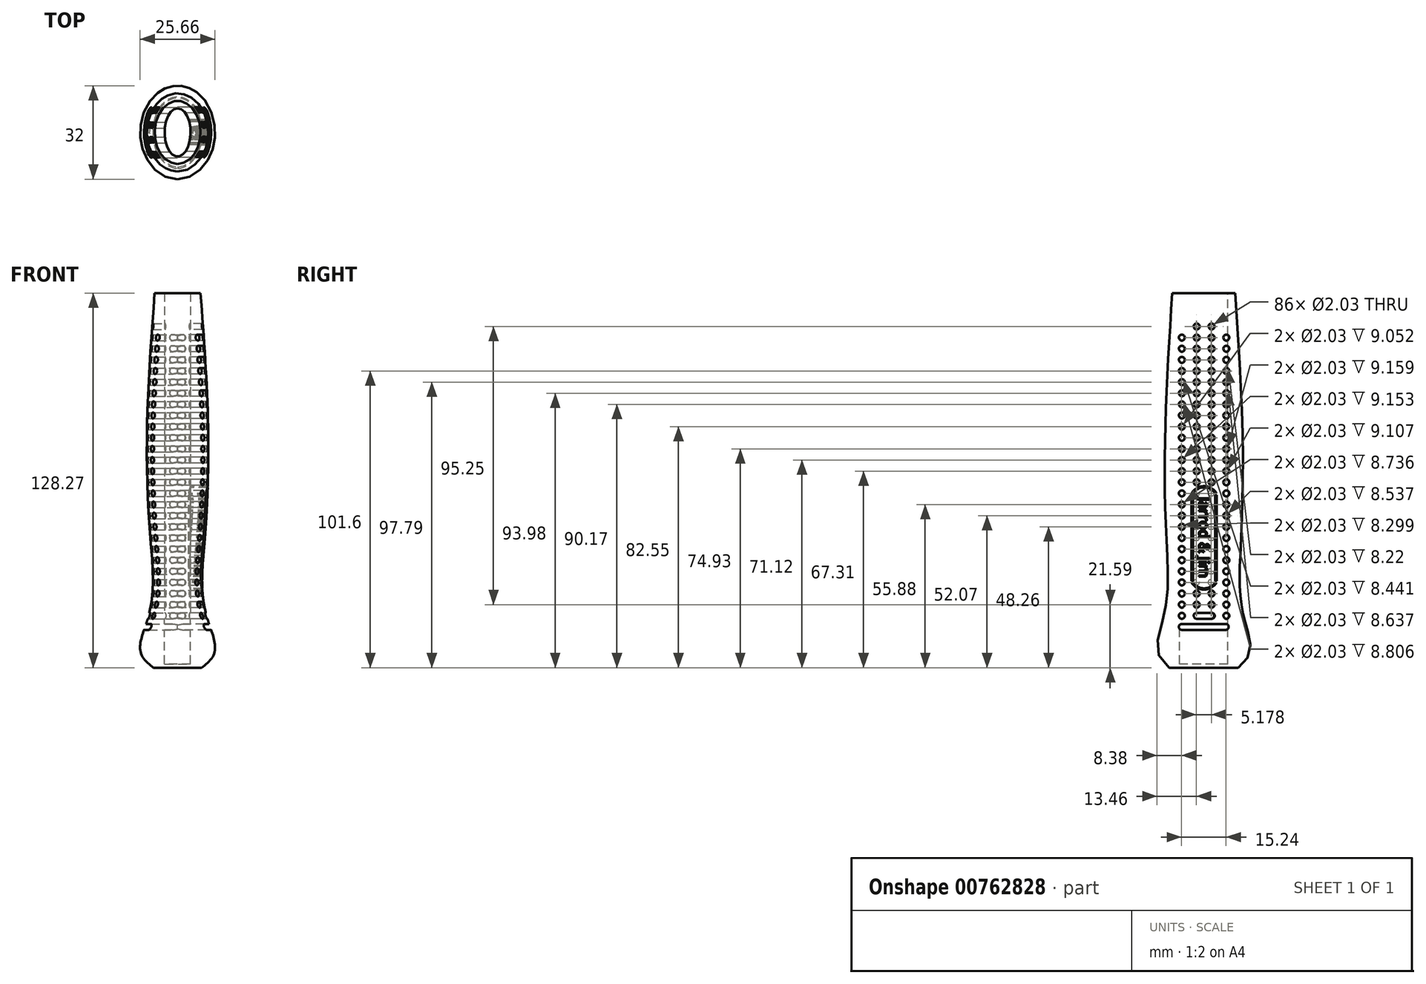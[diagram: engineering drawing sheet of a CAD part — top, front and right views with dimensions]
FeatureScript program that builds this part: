
annotation { "Feature Type Name" : "Feature", "Feature Type Description" : "" }
export const myFeature = defineFeature(function(context is Context, id is Id, definition is map)
    precondition{}
    {
        {
            var Q0;
            Q0=qCreatedBy(makeId("Top.planeOp"),FACE);
            var sketch = newSketch(context, id + "F0", { "sketchPlane" : qUnion([Q0])});
            skEllipse(sketch, "E0", {"center": v(0, 0) * mm, "majorRadius": 11.81 * mm, "minorRadius": 8.26 * mm, "majorAxis": v(0, -1)});
            skSolve(sketch);
        }
        {
            var Q0;
            Q0=qCreatedBy(makeId("Top.planeOp"),FACE);
            cPlane(context, id + "F1", {"entities" : qUnion([Q0]), "cplaneType" : CPlaneType.OFFSET, "offset" : 3.8 * mm, "width" : 152.4 * mm, "height" : 152.4 * mm});
        }
        {
            var Q0;
            Q0=qCreatedBy(id+"F1.planeOp",FACE);
            var sketch = newSketch(context, id + "F2", { "sketchPlane" : qUnion([Q0])});
            skEllipse(sketch, "E1", {"center": v(0, 0) * mm, "majorRadius": 15.24 * mm, "minorRadius": 12.07 * mm, "majorAxis": v(0, -1)});
            skSolve(sketch);
        }
        {
            var Q0;
            Q0=qCreatedBy(id+"F1.planeOp",FACE);
            cPlane(context, id + "F3", {"entities" : qUnion([Q0]), "cplaneType" : CPlaneType.OFFSET, "offset" : 12.7 * mm, "width" : 152.4 * mm, "height" : 152.4 * mm});
        }
        {
            var Q0;
            Q0=qCreatedBy(id+"F3.planeOp",FACE);
            var sketch = newSketch(context, id + "F4", { "sketchPlane" : qUnion([Q0])});
            skEllipse(sketch, "E2", {"center": v(0, 0) * mm, "majorRadius": 13.97 * mm, "minorRadius": 10.29 * mm, "majorAxis": v(0, -1)});
            skSolve(sketch);
        }
        {
            var Q0;
            Q0=qCreatedBy(id+"F3.planeOp",FACE);
            cPlane(context, id + "F5", {"entities" : qUnion([Q0]), "cplaneType" : CPlaneType.OFFSET, "offset" : 25.4 * mm, "width" : 152.4 * mm, "height" : 152.4 * mm});
        }
        {
            var Q0;
            Q0=qCreatedBy(id+"F5.planeOp",FACE);
            var sketch = newSketch(context, id + "F6", { "sketchPlane" : qUnion([Q0])});
            skEllipse(sketch, "E3", {"center": v(0, 0) * mm, "majorRadius": 12.7 * mm, "minorRadius": 9.14 * mm, "majorAxis": v(0, -1)});
            skSolve(sketch);
        }
        {
            var Q0;
            Q0=qCreatedBy(id+"F5.planeOp",FACE);
            cPlane(context, id + "F7", {"entities" : qUnion([Q0]), "cplaneType" : CPlaneType.OFFSET, "offset" : 33.02 * mm, "width" : 152.4 * mm, "height" : 152.4 * mm});
        }
        {
            var Q0;
            Q0=qCreatedBy(id+"F7.planeOp",FACE);
            var sketch = newSketch(context, id + "F8", { "sketchPlane" : qUnion([Q0])});
            skEllipse(sketch, "E4", {"center": v(0, 0) * mm, "majorRadius": 13.34 * mm, "minorRadius": 10.54 * mm, "majorAxis": v(0, -1)});
            skSolve(sketch);
        }
        {
            var Q0;
            Q0=qCreatedBy(id+"F7.planeOp",FACE);
            cPlane(context, id + "F9", {"entities" : qUnion([Q0]), "cplaneType" : CPlaneType.OFFSET, "offset" : 53.34 * mm, "width" : 152.4 * mm, "height" : 152.4 * mm});
        }
        {
            var Q0;
            Q0=qCreatedBy(id+"F9.planeOp",FACE);
            var sketch = newSketch(context, id + "F10", { "sketchPlane" : qUnion([Q0])});
            skEllipse(sketch, "E5", {"center": v(0, 0) * mm, "majorRadius": 10.8 * mm, "minorRadius": 7.87 * mm, "majorAxis": v(0, -1)});
            skSolve(sketch);
        }
        {
            var Q0;
            Q0=makeQuery(id+"F0.imprint","IMPRINT",FACE,{"disambiguationData":[TD([[makeQuery(id+"F0.imprint","IMPRINT",EDGE,{"derivedFrom":sQuery(id+"F0.wireOp",EDGE,"E0")}),1.0]])]});
            var Q1;
            Q1=makeQuery(id+"F2.imprint","IMPRINT",FACE,{"disambiguationData":[TD([[makeQuery(id+"F2.imprint","IMPRINT",EDGE,{"derivedFrom":sQuery(id+"F2.wireOp",EDGE,"E1")}),1.0]])]});
            var Q2;
            Q2=makeQuery(id+"F4.imprint","IMPRINT",FACE,{"disambiguationData":[TD([[makeQuery(id+"F4.imprint","IMPRINT",EDGE,{"derivedFrom":sQuery(id+"F4.wireOp",EDGE,"E2")}),1.0]])]});
            var Q3;
            Q3=makeQuery(id+"F6.imprint","IMPRINT",FACE,{"disambiguationData":[TD([[makeQuery(id+"F6.imprint","IMPRINT",EDGE,{"derivedFrom":sQuery(id+"F6.wireOp",EDGE,"E3")}),1.0]])]});
            var Q4;
            Q4=makeQuery(id+"F8.imprint","IMPRINT",FACE,{"disambiguationData":[TD([[makeQuery(id+"F8.imprint","IMPRINT",EDGE,{"derivedFrom":sQuery(id+"F8.wireOp",EDGE,"E4")}),1.0]])]});
            var Q5;
            Q5=makeQuery(id+"F10.imprint","IMPRINT",FACE,{"disambiguationData":[TD([[makeQuery(id+"F10.imprint","IMPRINT",EDGE,{"derivedFrom":sQuery(id+"F10.wireOp",EDGE,"E5")}),1.0]])]});
            loft(context, id + "F11", {"sheetProfilesArray" : [{ "sheetProfileEntities" : qUnion([Q0]) }, { "sheetProfileEntities" : qUnion([Q1]) }, { "sheetProfileEntities" : qUnion([Q2]) }, { "sheetProfileEntities" : qUnion([Q3]) }, { "sheetProfileEntities" : qUnion([Q4]) }, { "sheetProfileEntities" : qUnion([Q5]) }]});
        }
        {
            var Q0;
            Q0=makeQuery(id+"F11.opLoft","CAP_FACE",FACE,{"disambiguationData":[OSD([makeQuery(id+"F10.imprint","IMPRINT",FACE,{"disambiguationData":[TD([[makeQuery(id+"F10.imprint","IMPRINT",EDGE,{"derivedFrom":sQuery(id+"F10.wireOp",EDGE,"E5")}),1.0]])]})])],"isStart":true});
            var sketch = newSketch(context, id + "F12", { "sketchPlane" : qUnion([Q0])});
            skEllipse(sketch, "E6", {"center": v(0, 0) * mm, "majorRadius": 4.45 * mm, "minorRadius": 8.26 * mm, "majorAxis": v(1, 0)});
            skSolve(sketch);
        }
        {
            var Q0;
            Q0=makeQuery(id+"F12.imprint","IMPRINT",FACE,{"disambiguationData":[TD([[makeQuery(id+"F12.imprint","IMPRINT",EDGE,{"derivedFrom":sQuery(id+"F12.wireOp",EDGE,"E6")}),1.0]])]});
            extrude(context, id + "F13", {"entities" : qUnion([Q0]), "operationType" : NewBodyOperationType.REMOVE, "oppositeDirection" : true, "depth" : 127 * mm, "offsetDistance" : 25.4 * mm});
        }
        {
            var Q0;
            Q0=qCreatedBy(makeId("Right.planeOp"),FACE);
            var sketch = newSketch(context, id + "F14", { "sketchPlane" : qUnion([Q0])});
            skCircle(sketch, "E7", {"center": v(-7.62, 17.78) * mm, "radius": 1.02 * mm});
            skCircle(sketch, "E8.0.1.0", {"center": v(-7.62, 21.59) * mm, "radius": 1.02 * mm});
            skCircle(sketch, "E8.0.2.0", {"center": v(-7.62, 25.4) * mm, "radius": 1.02 * mm});
            skCircle(sketch, "E8.0.3.0", {"center": v(-7.62, 29.21) * mm, "radius": 1.02 * mm});
            skCircle(sketch, "E8.0.4.0", {"center": v(-7.62, 33.02) * mm, "radius": 1.02 * mm});
            skCircle(sketch, "E8.0.5.0", {"center": v(-7.62, 36.83) * mm, "radius": 1.02 * mm});
            skCircle(sketch, "E8.0.6.0", {"center": v(-7.62, 40.64) * mm, "radius": 1.02 * mm});
            skCircle(sketch, "E8.0.7.0", {"center": v(-7.62, 44.45) * mm, "radius": 1.02 * mm});
            skCircle(sketch, "E8.0.8.0", {"center": v(-7.62, 48.26) * mm, "radius": 1.02 * mm});
            skCircle(sketch, "E8.0.9.0", {"center": v(-7.62, 52.07) * mm, "radius": 1.02 * mm});
            skCircle(sketch, "E8.0.10.0", {"center": v(-7.62, 55.88) * mm, "radius": 1.02 * mm});
            skCircle(sketch, "E8.0.11.0", {"center": v(-7.62, 59.7) * mm, "radius": 1.02 * mm});
            skCircle(sketch, "E8.0.12.0", {"center": v(-7.62, 63.5) * mm, "radius": 1.02 * mm});
            skCircle(sketch, "E8.0.13.0", {"center": v(-7.62, 67.31) * mm, "radius": 1.02 * mm});
            skCircle(sketch, "E8.0.14.0", {"center": v(-7.62, 71.12) * mm, "radius": 1.02 * mm});
            skCircle(sketch, "E8.0.15.0", {"center": v(-7.62, 74.93) * mm, "radius": 1.02 * mm});
            skCircle(sketch, "E8.0.16.0", {"center": v(-7.62, 78.74) * mm, "radius": 1.02 * mm});
            skCircle(sketch, "E8.0.17.0", {"center": v(-7.62, 82.55) * mm, "radius": 1.02 * mm});
            skCircle(sketch, "E8.0.18.0", {"center": v(-7.62, 86.36) * mm, "radius": 1.02 * mm});
            skCircle(sketch, "E8.0.19.0", {"center": v(-7.62, 90.17) * mm, "radius": 1.02 * mm});
            skCircle(sketch, "E8.0.20.0", {"center": v(-7.62, 93.98) * mm, "radius": 1.02 * mm});
            skCircle(sketch, "E8.0.21.0", {"center": v(-7.62, 97.8) * mm, "radius": 1.02 * mm});
            skCircle(sketch, "E8.0.22.0", {"center": v(-7.62, 101.6) * mm, "radius": 1.02 * mm});
            skCircle(sketch, "E8.0.23.0", {"center": v(-7.62, 105.41) * mm, "radius": 1.02 * mm});
            skCircle(sketch, "E8.0.24.0", {"center": v(-7.62, 109.22) * mm, "radius": 1.02 * mm});
            skCircle(sketch, "E8.0.25.0", {"center": v(-7.62, 113.03) * mm, "radius": 1.02 * mm});
            skCircle(sketch, "E8.1.1.0", {"center": v(-2.54, 21.59) * mm, "radius": 1.02 * mm});
            skCircle(sketch, "E8.1.2.0", {"center": v(-2.54, 25.4) * mm, "radius": 1.02 * mm});
            skCircle(sketch, "E8.1.3.0", {"center": v(-2.54, 29.21) * mm, "radius": 1.02 * mm});
            skCircle(sketch, "E8.1.4.0", {"center": v(-2.54, 33.02) * mm, "radius": 1.02 * mm});
            skCircle(sketch, "E8.1.5.0", {"center": v(-2.54, 36.83) * mm, "radius": 1.02 * mm});
            skCircle(sketch, "E8.1.6.0", {"center": v(-2.54, 40.64) * mm, "radius": 1.02 * mm});
            skCircle(sketch, "E8.1.7.0", {"center": v(-2.54, 44.45) * mm, "radius": 1.02 * mm});
            skCircle(sketch, "E8.1.8.0", {"center": v(-2.54, 48.26) * mm, "radius": 1.02 * mm});
            skCircle(sketch, "E8.1.9.0", {"center": v(-2.54, 52.07) * mm, "radius": 1.02 * mm});
            skCircle(sketch, "E8.1.10.0", {"center": v(-2.54, 55.88) * mm, "radius": 1.02 * mm});
            skCircle(sketch, "E8.1.11.0", {"center": v(-2.54, 59.7) * mm, "radius": 1.02 * mm});
            skCircle(sketch, "E8.1.12.0", {"center": v(-2.54, 63.5) * mm, "radius": 1.02 * mm});
            skCircle(sketch, "E8.1.13.0", {"center": v(-2.54, 67.3) * mm, "radius": 1.02 * mm});
            skCircle(sketch, "E8.1.14.0", {"center": v(-2.54, 71.12) * mm, "radius": 1.02 * mm});
            skCircle(sketch, "E8.1.15.0", {"center": v(-2.54, 74.93) * mm, "radius": 1.02 * mm});
            skCircle(sketch, "E8.1.16.0", {"center": v(-2.54, 78.74) * mm, "radius": 1.02 * mm});
            skCircle(sketch, "E8.1.17.0", {"center": v(-2.54, 82.55) * mm, "radius": 1.02 * mm});
            skCircle(sketch, "E8.1.18.0", {"center": v(-2.54, 86.36) * mm, "radius": 1.02 * mm});
            skCircle(sketch, "E8.1.19.0", {"center": v(-2.54, 90.17) * mm, "radius": 1.02 * mm});
            skCircle(sketch, "E8.1.20.0", {"center": v(-2.54, 93.98) * mm, "radius": 1.02 * mm});
            skCircle(sketch, "E8.1.21.0", {"center": v(-2.54, 97.8) * mm, "radius": 1.02 * mm});
            skCircle(sketch, "E8.1.22.0", {"center": v(-2.54, 101.6) * mm, "radius": 1.02 * mm});
            skCircle(sketch, "E8.1.23.0", {"center": v(-2.54, 105.4) * mm, "radius": 1.02 * mm});
            skCircle(sketch, "E8.1.24.0", {"center": v(-2.54, 109.22) * mm, "radius": 1.02 * mm});
            skCircle(sketch, "E8.1.25.0", {"center": v(-2.54, 113.03) * mm, "radius": 1.02 * mm});
            skCircle(sketch, "E8.1.26.0", {"center": v(-2.54, 116.84) * mm, "radius": 1.02 * mm});
            skCircle(sketch, "E8.2.1.0", {"center": v(2.54, 21.59) * mm, "radius": 1.02 * mm});
            skCircle(sketch, "E8.2.2.0", {"center": v(2.54, 25.4) * mm, "radius": 1.02 * mm});
            skCircle(sketch, "E8.2.3.0", {"center": v(2.54, 29.21) * mm, "radius": 1.02 * mm});
            skCircle(sketch, "E8.2.4.0", {"center": v(2.54, 33.02) * mm, "radius": 1.02 * mm});
            skCircle(sketch, "E8.2.5.0", {"center": v(2.54, 36.83) * mm, "radius": 1.02 * mm});
            skCircle(sketch, "E8.2.6.0", {"center": v(2.54, 40.64) * mm, "radius": 1.02 * mm});
            skCircle(sketch, "E8.2.7.0", {"center": v(2.54, 44.45) * mm, "radius": 1.02 * mm});
            skCircle(sketch, "E8.2.8.0", {"center": v(2.54, 48.26) * mm, "radius": 1.02 * mm});
            skCircle(sketch, "E8.2.9.0", {"center": v(2.54, 52.07) * mm, "radius": 1.02 * mm});
            skCircle(sketch, "E8.2.10.0", {"center": v(2.54, 55.88) * mm, "radius": 1.02 * mm});
            skCircle(sketch, "E8.2.11.0", {"center": v(2.54, 59.7) * mm, "radius": 1.02 * mm});
            skCircle(sketch, "E8.2.12.0", {"center": v(2.54, 63.5) * mm, "radius": 1.02 * mm});
            skCircle(sketch, "E8.2.13.0", {"center": v(2.54, 67.3) * mm, "radius": 1.02 * mm});
            skCircle(sketch, "E8.2.14.0", {"center": v(2.54, 71.12) * mm, "radius": 1.02 * mm});
            skCircle(sketch, "E8.2.15.0", {"center": v(2.54, 74.93) * mm, "radius": 1.02 * mm});
            skCircle(sketch, "E8.2.16.0", {"center": v(2.54, 78.74) * mm, "radius": 1.02 * mm});
            skCircle(sketch, "E8.2.17.0", {"center": v(2.54, 82.55) * mm, "radius": 1.02 * mm});
            skCircle(sketch, "E8.2.18.0", {"center": v(2.54, 86.36) * mm, "radius": 1.02 * mm});
            skCircle(sketch, "E8.2.19.0", {"center": v(2.54, 90.17) * mm, "radius": 1.02 * mm});
            skCircle(sketch, "E8.2.20.0", {"center": v(2.54, 93.98) * mm, "radius": 1.02 * mm});
            skCircle(sketch, "E8.2.21.0", {"center": v(2.54, 97.8) * mm, "radius": 1.02 * mm});
            skCircle(sketch, "E8.2.22.0", {"center": v(2.54, 101.6) * mm, "radius": 1.02 * mm});
            skCircle(sketch, "E8.2.23.0", {"center": v(2.54, 105.4) * mm, "radius": 1.02 * mm});
            skCircle(sketch, "E8.2.24.0", {"center": v(2.54, 109.22) * mm, "radius": 1.02 * mm});
            skCircle(sketch, "E8.2.25.0", {"center": v(2.54, 113.03) * mm, "radius": 1.02 * mm});
            skCircle(sketch, "E8.2.26.0", {"center": v(2.54, 116.84) * mm, "radius": 1.02 * mm});
            skCircle(sketch, "E8.3.0.0", {"center": v(7.62, 17.78) * mm, "radius": 1.02 * mm});
            skCircle(sketch, "E8.3.1.0", {"center": v(7.62, 21.59) * mm, "radius": 1.02 * mm});
            skCircle(sketch, "E8.3.2.0", {"center": v(7.62, 25.4) * mm, "radius": 1.02 * mm});
            skCircle(sketch, "E8.3.3.0", {"center": v(7.62, 29.21) * mm, "radius": 1.02 * mm});
            skCircle(sketch, "E8.3.4.0", {"center": v(7.62, 33.02) * mm, "radius": 1.02 * mm});
            skCircle(sketch, "E8.3.5.0", {"center": v(7.62, 36.83) * mm, "radius": 1.02 * mm});
            skCircle(sketch, "E8.3.6.0", {"center": v(7.62, 40.64) * mm, "radius": 1.02 * mm});
            skCircle(sketch, "E8.3.7.0", {"center": v(7.62, 44.45) * mm, "radius": 1.02 * mm});
            skCircle(sketch, "E8.3.8.0", {"center": v(7.62, 48.26) * mm, "radius": 1.02 * mm});
            skCircle(sketch, "E8.3.9.0", {"center": v(7.62, 52.07) * mm, "radius": 1.02 * mm});
            skCircle(sketch, "E8.3.10.0", {"center": v(7.62, 55.88) * mm, "radius": 1.02 * mm});
            skCircle(sketch, "E8.3.11.0", {"center": v(7.62, 59.7) * mm, "radius": 1.02 * mm});
            skCircle(sketch, "E8.3.12.0", {"center": v(7.62, 63.5) * mm, "radius": 1.02 * mm});
            skCircle(sketch, "E8.3.13.0", {"center": v(7.62, 67.3) * mm, "radius": 1.02 * mm});
            skCircle(sketch, "E8.3.14.0", {"center": v(7.62, 71.12) * mm, "radius": 1.02 * mm});
            skCircle(sketch, "E8.3.15.0", {"center": v(7.62, 74.93) * mm, "radius": 1.02 * mm});
            skCircle(sketch, "E8.3.16.0", {"center": v(7.62, 78.74) * mm, "radius": 1.02 * mm});
            skCircle(sketch, "E8.3.17.0", {"center": v(7.62, 82.55) * mm, "radius": 1.02 * mm});
            skCircle(sketch, "E8.3.18.0", {"center": v(7.62, 86.36) * mm, "radius": 1.02 * mm});
            skCircle(sketch, "E8.3.19.0", {"center": v(7.62, 90.17) * mm, "radius": 1.02 * mm});
            skCircle(sketch, "E8.3.20.0", {"center": v(7.62, 93.98) * mm, "radius": 1.02 * mm});
            skCircle(sketch, "E8.3.21.0", {"center": v(7.62, 97.8) * mm, "radius": 1.02 * mm});
            skCircle(sketch, "E8.3.22.0", {"center": v(7.62, 101.6) * mm, "radius": 1.02 * mm});
            skCircle(sketch, "E8.3.23.0", {"center": v(7.62, 105.4) * mm, "radius": 1.02 * mm});
            skCircle(sketch, "E8.3.24.0", {"center": v(7.62, 109.22) * mm, "radius": 1.02 * mm});
            skCircle(sketch, "E8.3.25.0", {"center": v(7.62, 113.03) * mm, "radius": 1.02 * mm});
            skLineSegment(sketch, "E8.direction1", {"start": v(-7.62, 17.78) * mm, "end": v(-2.54, 17.78) * mm, "construction": true});
            skLineSegment(sketch, "E8.direction2", {"start": v(-7.62, 17.78) * mm, "end": v(-7.62, 21.59) * mm, "construction": true});
            skLineSegment(sketch, "E9.bottom", {"start": v(-2.54, 16.76) * mm, "end": v(2.54, 16.76) * mm});
            skLineSegment(sketch, "E9.top", {"start": v(-2.54, 18.8) * mm, "end": v(2.54, 18.8) * mm});
            skLineSegment(sketch, "E9.left", {"start": v(-2.54, 16.76) * mm, "end": v(-2.54, 18.8) * mm});
            skLineSegment(sketch, "E9.right", {"start": v(2.54, 16.76) * mm, "end": v(2.54, 18.8) * mm});
            skPoint(sketch, "E9.middle", {"position": v(0, 17.78) * mm});
            skArc(sketch, "E10", {"start": v(2.54, 16.76) * mm, "mid": v(3.56, 17.78) * mm, "end": v(2.54, 18.8) * mm});
            skArc(sketch, "E11", {"start": v(-2.54, 18.8) * mm, "mid": v(-3.56, 17.78) * mm, "end": v(-2.54, 16.76) * mm});
            skLineSegment(sketch, "E12.bottom", {"start": v(-7.62, 12.95) * mm, "end": v(7.62, 12.95) * mm});
            skLineSegment(sketch, "E12.top", {"start": v(-7.62, 14.99) * mm, "end": v(7.62, 14.99) * mm});
            skLineSegment(sketch, "E12.left", {"start": v(-7.62, 12.95) * mm, "end": v(-7.62, 14.99) * mm});
            skLineSegment(sketch, "E12.right", {"start": v(7.62, 12.95) * mm, "end": v(7.62, 14.99) * mm});
            skPoint(sketch, "E12.middle", {"position": v(0, 13.97) * mm});
            skArc(sketch, "E13", {"start": v(-7.62, 14.99) * mm, "mid": v(-8.64, 13.97) * mm, "end": v(-7.62, 12.95) * mm});
            skArc(sketch, "E14", {"start": v(7.62, 12.95) * mm, "mid": v(8.64, 13.97) * mm, "end": v(7.62, 14.99) * mm});
            skSolve(sketch);
        }
        {
            var Q0;
            Q0 = qSketchRegion(id + "F14", true);
            extrude(context, id + "F15", {"entities" : qUnion([Q0]), "operationType" : NewBodyOperationType.REMOVE, "endBound" : BoundingType.THROUGH_ALL, "oppositeDirection" : true, "depth" : 25.4 * mm, "offsetDistance" : 25.4 * mm});
        }
        {
            var Q0;
            Q0=qCreatedBy(makeId("Right.planeOp"),FACE);
            var sketch = newSketch(context, id + "F16", { "sketchPlane" : qUnion([Q0])});
            skCircle(sketch, "E15", {"center": v(-7.52, 17.78) * mm, "radius": 1.02 * mm});
            skCircle(sketch, "E16.0.1.0", {"center": v(-7.52, 21.59) * mm, "radius": 1.02 * mm});
            skCircle(sketch, "E16.0.2.0", {"center": v(-7.52, 25.4) * mm, "radius": 1.02 * mm});
            skCircle(sketch, "E16.0.3.0", {"center": v(-7.52, 29.2) * mm, "radius": 1.02 * mm});
            skCircle(sketch, "E16.0.4.0", {"center": v(-7.52, 33.02) * mm, "radius": 1.02 * mm});
            skCircle(sketch, "E16.0.5.0", {"center": v(-7.52, 36.83) * mm, "radius": 1.02 * mm});
            skCircle(sketch, "E16.0.6.0", {"center": v(-7.52, 40.64) * mm, "radius": 1.02 * mm});
            skCircle(sketch, "E16.0.7.0", {"center": v(-7.52, 44.45) * mm, "radius": 1.02 * mm});
            skCircle(sketch, "E16.0.8.0", {"center": v(-7.52, 48.26) * mm, "radius": 1.02 * mm});
            skCircle(sketch, "E16.0.9.0", {"center": v(-7.52, 52.07) * mm, "radius": 1.02 * mm});
            skCircle(sketch, "E16.0.10.0", {"center": v(-7.52, 55.88) * mm, "radius": 1.02 * mm});
            skCircle(sketch, "E16.0.11.0", {"center": v(-7.52, 59.69) * mm, "radius": 1.02 * mm});
            skCircle(sketch, "E16.0.12.0", {"center": v(-7.52, 63.5) * mm, "radius": 1.02 * mm});
            skCircle(sketch, "E16.0.13.0", {"center": v(-7.52, 67.3) * mm, "radius": 1.02 * mm});
            skCircle(sketch, "E16.0.14.0", {"center": v(-7.52, 71.12) * mm, "radius": 1.02 * mm});
            skCircle(sketch, "E16.0.15.0", {"center": v(-7.52, 74.93) * mm, "radius": 1.02 * mm});
            skCircle(sketch, "E16.0.16.0", {"center": v(-7.52, 78.74) * mm, "radius": 1.02 * mm});
            skCircle(sketch, "E16.0.17.0", {"center": v(-7.52, 82.55) * mm, "radius": 1.02 * mm});
            skCircle(sketch, "E16.0.18.0", {"center": v(-7.52, 86.36) * mm, "radius": 1.02 * mm});
            skCircle(sketch, "E16.0.19.0", {"center": v(-7.52, 90.17) * mm, "radius": 1.02 * mm});
            skCircle(sketch, "E16.0.20.0", {"center": v(-7.52, 93.98) * mm, "radius": 1.02 * mm});
            skCircle(sketch, "E16.0.21.0", {"center": v(-7.52, 97.79) * mm, "radius": 1.02 * mm});
            skCircle(sketch, "E16.0.22.0", {"center": v(-7.52, 101.6) * mm, "radius": 1.02 * mm});
            skCircle(sketch, "E16.0.23.0", {"center": v(-7.52, 105.4) * mm, "radius": 1.02 * mm});
            skCircle(sketch, "E16.0.24.0", {"center": v(-7.52, 109.22) * mm, "radius": 1.02 * mm});
            skCircle(sketch, "E16.0.25.0", {"center": v(-7.52, 113.03) * mm, "radius": 1.02 * mm});
            skCircle(sketch, "E16.1.1.0", {"center": v(-2.44, 21.59) * mm, "radius": 1.02 * mm});
            skCircle(sketch, "E16.1.2.0", {"center": v(-2.44, 25.4) * mm, "radius": 1.02 * mm});
            skCircle(sketch, "E16.1.12.0", {"center": v(-2.44, 63.5) * mm, "radius": 1.02 * mm});
            skCircle(sketch, "E16.1.13.0", {"center": v(-2.44, 67.3) * mm, "radius": 1.02 * mm});
            skCircle(sketch, "E16.1.14.0", {"center": v(-2.44, 71.12) * mm, "radius": 1.02 * mm});
            skCircle(sketch, "E16.1.15.0", {"center": v(-2.44, 74.93) * mm, "radius": 1.02 * mm});
            skCircle(sketch, "E16.1.16.0", {"center": v(-2.44, 78.74) * mm, "radius": 1.02 * mm});
            skCircle(sketch, "E16.1.17.0", {"center": v(-2.44, 82.55) * mm, "radius": 1.02 * mm});
            skCircle(sketch, "E16.1.18.0", {"center": v(-2.44, 86.36) * mm, "radius": 1.02 * mm});
            skCircle(sketch, "E16.1.19.0", {"center": v(-2.44, 90.17) * mm, "radius": 1.02 * mm});
            skCircle(sketch, "E16.1.20.0", {"center": v(-2.44, 93.98) * mm, "radius": 1.02 * mm});
            skCircle(sketch, "E16.1.21.0", {"center": v(-2.44, 97.79) * mm, "radius": 1.02 * mm});
            skCircle(sketch, "E16.1.22.0", {"center": v(-2.44, 101.6) * mm, "radius": 1.02 * mm});
            skCircle(sketch, "E16.1.23.0", {"center": v(-2.44, 105.4) * mm, "radius": 1.02 * mm});
            skCircle(sketch, "E16.1.24.0", {"center": v(-2.44, 109.22) * mm, "radius": 1.02 * mm});
            skCircle(sketch, "E16.1.25.0", {"center": v(-2.44, 113.03) * mm, "radius": 1.02 * mm});
            skCircle(sketch, "E16.1.26.0", {"center": v(-2.44, 116.84) * mm, "radius": 1.02 * mm});
            skCircle(sketch, "E16.2.1.0", {"center": v(2.64, 21.59) * mm, "radius": 1.02 * mm});
            skCircle(sketch, "E16.2.2.0", {"center": v(2.64, 25.4) * mm, "radius": 1.02 * mm});
            skCircle(sketch, "E16.2.12.0", {"center": v(2.64, 63.5) * mm, "radius": 1.02 * mm});
            skCircle(sketch, "E16.2.13.0", {"center": v(2.64, 67.3) * mm, "radius": 1.02 * mm});
            skCircle(sketch, "E16.2.14.0", {"center": v(2.64, 71.12) * mm, "radius": 1.02 * mm});
            skCircle(sketch, "E16.2.15.0", {"center": v(2.64, 74.93) * mm, "radius": 1.02 * mm});
            skCircle(sketch, "E16.2.16.0", {"center": v(2.64, 78.74) * mm, "radius": 1.02 * mm});
            skCircle(sketch, "E16.2.17.0", {"center": v(2.64, 82.55) * mm, "radius": 1.02 * mm});
            skCircle(sketch, "E16.2.18.0", {"center": v(2.64, 86.36) * mm, "radius": 1.02 * mm});
            skCircle(sketch, "E16.2.19.0", {"center": v(2.64, 90.17) * mm, "radius": 1.02 * mm});
            skCircle(sketch, "E16.2.20.0", {"center": v(2.64, 93.98) * mm, "radius": 1.02 * mm});
            skCircle(sketch, "E16.2.21.0", {"center": v(2.64, 97.79) * mm, "radius": 1.02 * mm});
            skCircle(sketch, "E16.2.22.0", {"center": v(2.64, 101.6) * mm, "radius": 1.02 * mm});
            skCircle(sketch, "E16.2.23.0", {"center": v(2.64, 105.4) * mm, "radius": 1.02 * mm});
            skCircle(sketch, "E16.2.24.0", {"center": v(2.64, 109.22) * mm, "radius": 1.02 * mm});
            skCircle(sketch, "E16.2.25.0", {"center": v(2.64, 113.03) * mm, "radius": 1.02 * mm});
            skCircle(sketch, "E16.2.26.0", {"center": v(2.64, 116.84) * mm, "radius": 1.02 * mm});
            skCircle(sketch, "E16.3.0.0", {"center": v(7.72, 17.78) * mm, "radius": 1.02 * mm});
            skCircle(sketch, "E16.3.1.0", {"center": v(7.72, 21.59) * mm, "radius": 1.02 * mm});
            skCircle(sketch, "E16.3.2.0", {"center": v(7.72, 25.4) * mm, "radius": 1.02 * mm});
            skCircle(sketch, "E16.3.3.0", {"center": v(7.72, 29.2) * mm, "radius": 1.02 * mm});
            skCircle(sketch, "E16.3.4.0", {"center": v(7.72, 33.02) * mm, "radius": 1.02 * mm});
            skCircle(sketch, "E16.3.5.0", {"center": v(7.72, 36.83) * mm, "radius": 1.02 * mm});
            skCircle(sketch, "E16.3.6.0", {"center": v(7.72, 40.64) * mm, "radius": 1.02 * mm});
            skCircle(sketch, "E16.3.7.0", {"center": v(7.72, 44.45) * mm, "radius": 1.02 * mm});
            skCircle(sketch, "E16.3.8.0", {"center": v(7.72, 48.26) * mm, "radius": 1.02 * mm});
            skCircle(sketch, "E16.3.9.0", {"center": v(7.72, 52.07) * mm, "radius": 1.02 * mm});
            skCircle(sketch, "E16.3.10.0", {"center": v(7.72, 55.88) * mm, "radius": 1.02 * mm});
            skCircle(sketch, "E16.3.11.0", {"center": v(7.72, 59.69) * mm, "radius": 1.02 * mm});
            skCircle(sketch, "E16.3.12.0", {"center": v(7.72, 63.5) * mm, "radius": 1.02 * mm});
            skCircle(sketch, "E16.3.13.0", {"center": v(7.72, 67.3) * mm, "radius": 1.02 * mm});
            skCircle(sketch, "E16.3.14.0", {"center": v(7.72, 71.12) * mm, "radius": 1.02 * mm});
            skCircle(sketch, "E16.3.15.0", {"center": v(7.72, 74.93) * mm, "radius": 1.02 * mm});
            skCircle(sketch, "E16.3.16.0", {"center": v(7.72, 78.74) * mm, "radius": 1.02 * mm});
            skCircle(sketch, "E16.3.17.0", {"center": v(7.72, 82.55) * mm, "radius": 1.02 * mm});
            skCircle(sketch, "E16.3.18.0", {"center": v(7.72, 86.36) * mm, "radius": 1.02 * mm});
            skCircle(sketch, "E16.3.19.0", {"center": v(7.72, 90.17) * mm, "radius": 1.02 * mm});
            skCircle(sketch, "E16.3.20.0", {"center": v(7.72, 93.98) * mm, "radius": 1.02 * mm});
            skCircle(sketch, "E16.3.21.0", {"center": v(7.72, 97.79) * mm, "radius": 1.02 * mm});
            skCircle(sketch, "E16.3.22.0", {"center": v(7.72, 101.6) * mm, "radius": 1.02 * mm});
            skCircle(sketch, "E16.3.23.0", {"center": v(7.72, 105.4) * mm, "radius": 1.02 * mm});
            skCircle(sketch, "E16.3.24.0", {"center": v(7.72, 109.22) * mm, "radius": 1.02 * mm});
            skCircle(sketch, "E16.3.25.0", {"center": v(7.72, 113.03) * mm, "radius": 1.02 * mm});
            skLineSegment(sketch, "E16.direction1", {"start": v(-7.52, 17.78) * mm, "end": v(-2.44, 17.78) * mm, "construction": true});
            skLineSegment(sketch, "E16.direction2", {"start": v(-7.52, 17.78) * mm, "end": v(-7.52, 21.59) * mm, "construction": true});
            skLineSegment(sketch, "E17.bottom", {"start": v(-2.44, 16.76) * mm, "end": v(2.73, 16.76) * mm});
            skLineSegment(sketch, "E17.top", {"start": v(-2.44, 18.8) * mm, "end": v(2.73, 18.8) * mm});
            skLineSegment(sketch, "E17.left", {"start": v(-2.44, 16.76) * mm, "end": v(-2.44, 18.8) * mm});
            skLineSegment(sketch, "E17.right", {"start": v(2.73, 16.76) * mm, "end": v(2.73, 18.8) * mm});
            skPoint(sketch, "E17.middle", {"position": v(0.14, 17.78) * mm});
            skArc(sketch, "E18", {"start": v(2.73, 16.76) * mm, "mid": v(3.74, 17.78) * mm, "end": v(2.73, 18.8) * mm});
            skArc(sketch, "E19", {"start": v(-2.44, 18.8) * mm, "mid": v(-3.46, 17.78) * mm, "end": v(-2.44, 16.76) * mm});
            skLineSegment(sketch, "E20.bottom", {"start": v(-7.52, 12.95) * mm, "end": v(7.52, 12.95) * mm});
            skLineSegment(sketch, "E20.top", {"start": v(-7.52, 14.99) * mm, "end": v(7.52, 14.99) * mm});
            skLineSegment(sketch, "E20.left", {"start": v(-7.52, 12.95) * mm, "end": v(-7.52, 14.99) * mm});
            skLineSegment(sketch, "E20.right", {"start": v(7.52, 12.95) * mm, "end": v(7.52, 14.99) * mm});
            skPoint(sketch, "E20.middle", {"position": v(0, 13.97) * mm});
            skArc(sketch, "E21", {"start": v(-7.52, 14.99) * mm, "mid": v(-8.54, 13.97) * mm, "end": v(-7.52, 12.95) * mm});
            skArc(sketch, "E22", {"start": v(7.52, 12.95) * mm, "mid": v(8.54, 13.97) * mm, "end": v(7.52, 14.99) * mm});
            skText(sketch, "E23", { "text": "Jarrod & Jim", "fontName": "OpenSans-Regular.ttf"});
            skPoint(sketch, "E24", {"position": v(0.14, 30.48) * mm});
            skLineSegment(sketch, "E25.bottom", {"start": v(3.9, 59.18) * mm, "end": v(-3.71, 59.18) * mm, "construction": true});
            skLineSegment(sketch, "E25.top", {"start": v(3.9, 29.72) * mm, "end": v(-3.71, 29.72) * mm, "construction": true});
            skLineSegment(sketch, "E25.left", {"start": v(3.9, 59.18) * mm, "end": v(3.9, 29.72) * mm, "construction": true});
            skLineSegment(sketch, "E25.right", {"start": v(-3.71, 59.18) * mm, "end": v(-3.71, 29.72) * mm, "construction": true});
            skLineSegment(sketch, "E26.bottom", {"start": v(-3.71, 59.18) * mm, "end": v(-4.22, 59.18) * mm});
            skLineSegment(sketch, "E26.top", {"start": v(-3.71, 29.72) * mm, "end": v(-4.22, 29.72) * mm});
            skLineSegment(sketch, "E26.left", {"start": v(-3.71, 59.18) * mm, "end": v(-3.71, 29.72) * mm});
            skLineSegment(sketch, "E26.right", {"start": v(-4.22, 59.18) * mm, "end": v(-4.22, 29.72) * mm});
            skLineSegment(sketch, "E27.bottom", {"start": v(3.9, 59.18) * mm, "end": v(4.42, 59.18) * mm});
            skLineSegment(sketch, "E27.top", {"start": v(3.9, 29.72) * mm, "end": v(4.42, 29.72) * mm});
            skLineSegment(sketch, "E27.left", {"start": v(3.9, 59.18) * mm, "end": v(3.9, 29.72) * mm});
            skLineSegment(sketch, "E27.right", {"start": v(4.42, 59.18) * mm, "end": v(4.42, 29.72) * mm});
            skArc(sketch, "E28", {"start": v(3.9, 59.69) * mm, "mid": v(0.1, 61.73) * mm, "end": v(-3.71, 59.69) * mm});
            skArc(sketch, "E29", {"start": v(4.42, 59.69) * mm, "mid": v(0.1, 62.17) * mm, "end": v(-4.22, 59.69) * mm});
            skLineSegment(sketch, "E30", {"start": v(4.42, 59.69) * mm, "end": v(3.9, 59.69) * mm});
            skLineSegment(sketch, "E31", {"start": v(-4.22, 59.69) * mm, "end": v(-3.71, 59.69) * mm});
            skArc(sketch, "E32.MirrorCS", {"start": v(3.9, 29.2) * mm, "mid": v(0.1, 27.17) * mm, "end": v(-3.71, 29.2) * mm});
            skArc(sketch, "E33.MirrorCS", {"start": v(4.42, 29.21) * mm, "mid": v(0.1, 26.73) * mm, "end": v(-4.22, 29.2) * mm});
            skLineSegment(sketch, "E34.MirrorCS", {"start": v(4.42, 29.2) * mm, "end": v(3.9, 29.2) * mm});
            skLineSegment(sketch, "E35.MirrorCS", {"start": v(-4.22, 29.2) * mm, "end": v(-3.71, 29.2) * mm});
            const initialGuessF16  = {"E23": [-0.00165, 0.05842, 0, -1, 0.00358]};
            skSetInitialGuess(sketch, initialGuessF16);
            skSolve(sketch);
        }
        {
            var Q0;
            Q0 = qSketchRegion(id + "F16", true);
            extrude(context, id + "F17", {"entities" : qUnion([Q0]), "operationType" : NewBodyOperationType.REMOVE, "depth" : 25.4 * mm, "offsetDistance" : 25.4 * mm});
        }
    });
